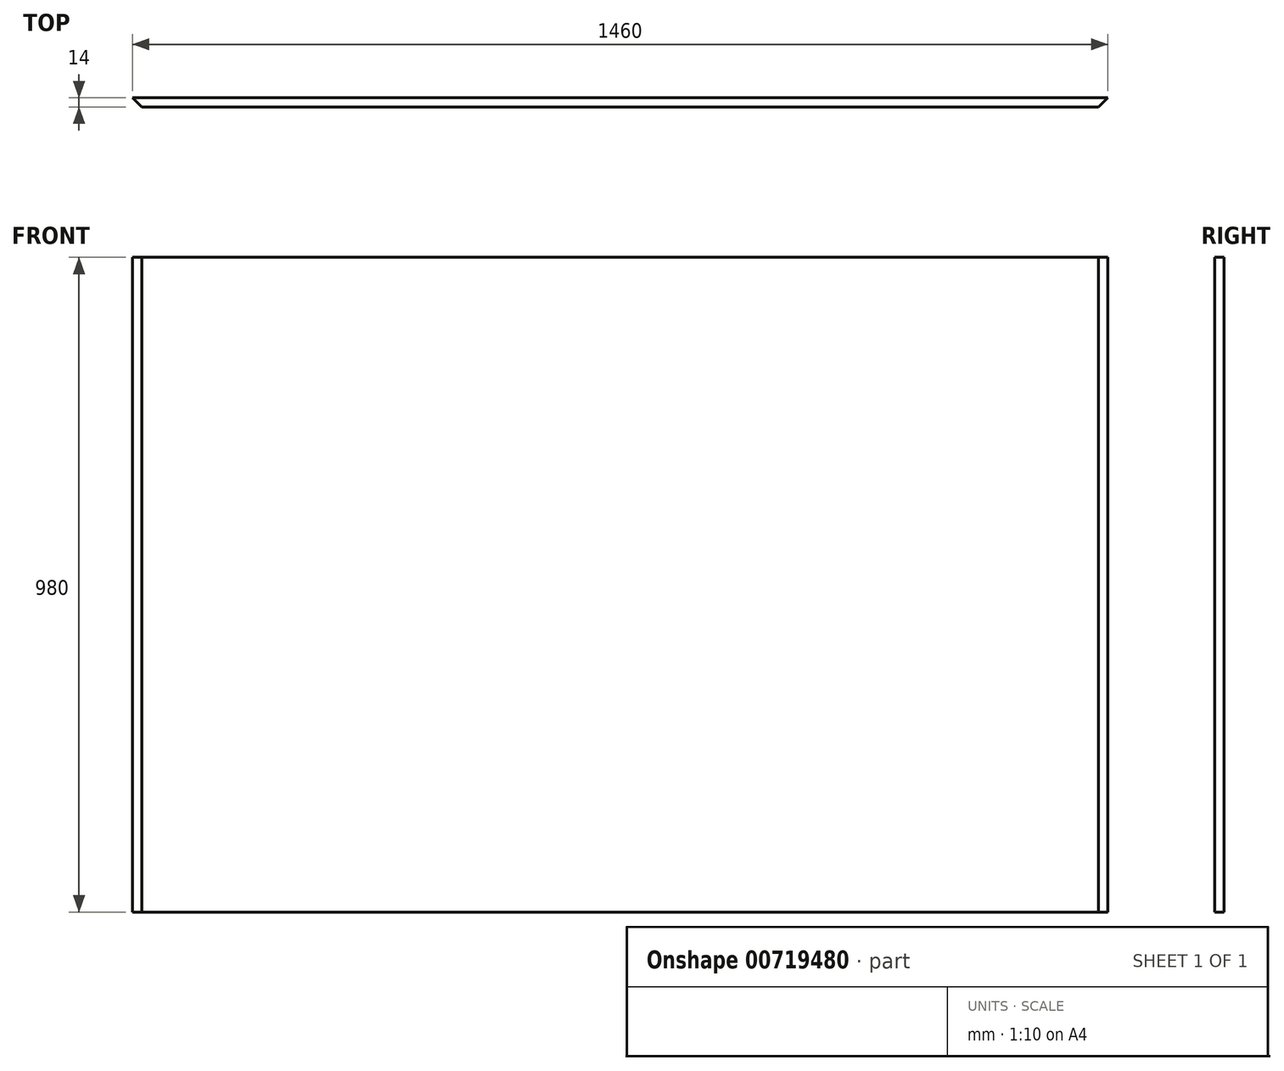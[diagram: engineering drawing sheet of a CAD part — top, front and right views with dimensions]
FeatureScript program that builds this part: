
annotation { "Feature Type Name" : "Feature", "Feature Type Description" : "" }
export const myFeature = defineFeature(function(context is Context, id is Id, definition is map)
    precondition{}
    {
        {
            var Q0;
            Q0=qCreatedBy(makeId("Front.planeOp"),FACE);
            var sketch = newSketch(context, id + "F0", { "sketchPlane" : qUnion([Q0])});
            skLineSegment(sketch, "E0.bottom", {"start": v(730, 490) * mm, "end": v(-730, 490) * mm});
            skLineSegment(sketch, "E0.top", {"start": v(730, -490) * mm, "end": v(-730, -490) * mm});
            skLineSegment(sketch, "E0.left", {"start": v(730, 490) * mm, "end": v(730, -490) * mm});
            skLineSegment(sketch, "E0.right", {"start": v(-730, 490) * mm, "end": v(-730, -490) * mm});
            skPoint(sketch, "E0.middle", {"position": v(0, 0) * mm});
            skSolve(sketch);
        }
        {
            var Q0;
            Q0=makeQuery(id+"F0.imprint","IMPRINT",FACE,{"disambiguationData":[TD([[makeQuery(id+"F0.imprint","IMPRINT",EDGE,{"derivedFrom":sQuery(id+"F0.wireOp",EDGE,"E0.bottom")}),1.0]])]});
            extrude(context, id + "F1", {"entities" : qUnion([Q0]), "depth" : 14 * mm, "offsetDistance" : 25 * mm});
        }
        {
            var Q0;
            Q0=makeQuery(id+"F1.opExtrude","CAP_EDGE",EDGE,{"disambiguationData":[OSD([sQuery(id+"F0.wireOp",EDGE,"E0.right")])],"isStart":false});
            var Q1;
            Q1=makeQuery(id+"F1.opExtrude","CAP_EDGE",EDGE,{"disambiguationData":[OSD([sQuery(id+"F0.wireOp",EDGE,"E0.left")])],"isStart":false});
            chamfer(context, id + "F2", {"entities" : qUnion([Q0, Q1]), "width" : 14 * mm, "tangentPropagation" : true});
        }
    });
